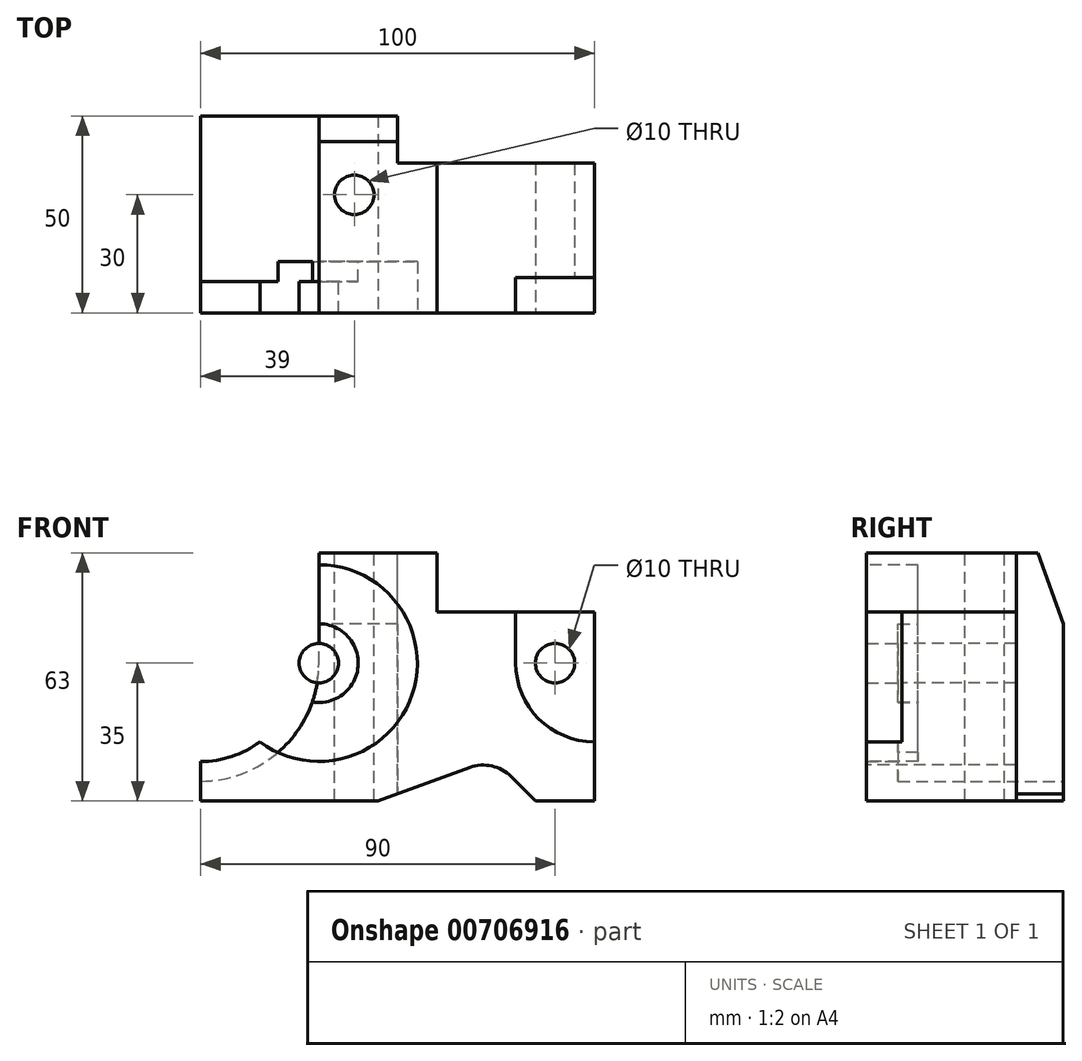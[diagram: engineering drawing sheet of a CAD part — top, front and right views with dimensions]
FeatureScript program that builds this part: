
annotation { "Feature Type Name" : "Feature", "Feature Type Description" : "" }
export const myFeature = defineFeature(function(context is Context, id is Id, definition is map)
    precondition{}
    {
        {
            var Q0;
            Q0=qCreatedBy(makeId("Front.planeOp"),FACE);
            var sketch = newSketch(context, id + "F0", { "sketchPlane" : qUnion([Q0])});
            skLineSegment(sketch, "E0", {"start": v(0, 0) * mm, "end": v(100, 0) * mm});
            skLineSegment(sketch, "E1", {"start": v(100, 0) * mm, "end": v(100, 63) * mm});
            skLineSegment(sketch, "E2", {"start": v(100, 63) * mm, "end": v(0, 63) * mm});
            skLineSegment(sketch, "E3", {"start": v(0, 63) * mm, "end": v(0, 0) * mm});
            skSolve(sketch);
        }
        {
            var Q0;
            Q0 = qSketchRegion(id + "F0", true);
            extrude(context, id + "F1", {"entities" : qUnion([Q0]), "depth" : 50 * mm, "offsetDistance" : 25 * mm});
        }
        {
            var Q0;
            Q0=makeQuery(id+"F1.opExtrude","CAP_FACE",FACE,{"disambiguationData":[OSD([sQuery(id+"F0.wireOp",EDGE,"E0"),sQuery(id+"F0.wireOp",EDGE,"E1"),sQuery(id+"F0.wireOp",EDGE,"E2"),sQuery(id+"F0.wireOp",EDGE,"E3")])],"isStart":false});
            var sketch = newSketch(context, id + "F2", { "sketchPlane" : qUnion([Q0])});
            skLineSegment(sketch, "E4", {"start": v(100, 48) * mm, "end": v(60, 48) * mm});
            skLineSegment(sketch, "E5", {"start": v(60, 48) * mm, "end": v(60, 63) * mm});
            skLineSegment(sketch, "E6", {"start": v(60, 63) * mm, "end": v(100, 63) * mm});
            skLineSegment(sketch, "E7", {"start": v(100, 63) * mm, "end": v(100, 48) * mm});
            skSolve(sketch);
        }
        {
            var Q0;
            Q0 = qSketchRegion(id + "F2", true);
            extrude(context, id + "F3", {"entities" : qUnion([Q0]), "operationType" : NewBodyOperationType.REMOVE, "endBound" : BoundingType.THROUGH_ALL, "oppositeDirection" : true, "depth" : 25 * mm, "offsetDistance" : 25 * mm});
        }
        {
            var Q0;
            Q0=makeQuery(id+"F1.opExtrude","CAP_FACE",FACE,{"disambiguationData":[OSD([sQuery(id+"F0.wireOp",EDGE,"E0"),sQuery(id+"F0.wireOp",EDGE,"E1"),sQuery(id+"F0.wireOp",EDGE,"E2"),sQuery(id+"F0.wireOp",EDGE,"E3")])],"isStart":true});
            var sketch = newSketch(context, id + "F4", { "sketchPlane" : qUnion([Q0])});
            skCircle(sketch, "E8", {"center": v(0, 35) * mm, "radius": 30 * mm});
            skLineSegment(sketch, "E9", {"start": v(-30, 35) * mm, "end": v(-30, 65) * mm});
            skLineSegment(sketch, "E10", {"start": v(-30, 65) * mm, "end": v(0, 65) * mm});
            skSolve(sketch);
        }
        {
            var Q0;
            Q0 = qSketchRegion(id + "F4", true);
            extrude(context, id + "F5", {"entities" : qUnion([Q0]), "operationType" : NewBodyOperationType.REMOVE, "oppositeDirection" : true, "depth" : 42 * mm, "offsetDistance" : 25 * mm});
        }
        {
            var Q0;
            Q0=makeQuery(id+"F1.opExtrude","CAP_FACE",FACE,{"disambiguationData":[OSD([sQuery(id+"F0.wireOp",EDGE,"E0"),sQuery(id+"F0.wireOp",EDGE,"E1"),sQuery(id+"F0.wireOp",EDGE,"E2"),sQuery(id+"F0.wireOp",EDGE,"E3")])],"isStart":true});
            var sketch = newSketch(context, id + "F6", { "sketchPlane" : qUnion([Q0])});
            skArc(sketch, "E11.0", {"start": v(-30, 35) * mm, "mid": v(-21.21, 13.79) * mm, "end": v(0, 5) * mm});
            skCircle(sketch, "E12", {"center": v(0, 35) * mm, "radius": 25 * mm});
            skSolve(sketch);
        }
        {
            var Q0;
            Q0 = qSketchRegion(id + "F6", true);
            extrude(context, id + "F7", {"entities" : qUnion([Q0]), "operationType" : NewBodyOperationType.REMOVE, "endBound" : BoundingType.THROUGH_ALL, "oppositeDirection" : true, "depth" : 25 * mm, "offsetDistance" : 25 * mm});
        }
        {
            var Q0;
            Q0=makeQuery(id+"F1.opExtrude","CAP_FACE",FACE,{"disambiguationData":[OSD([sQuery(id+"F0.wireOp",EDGE,"E0"),sQuery(id+"F0.wireOp",EDGE,"E1"),sQuery(id+"F0.wireOp",EDGE,"E2"),sQuery(id+"F0.wireOp",EDGE,"E3")])],"isStart":true});
            var sketch = newSketch(context, id + "F8", { "sketchPlane" : qUnion([Q0])});
            skLineSegment(sketch, "E13.0", {"start": v(-30, 35) * mm, "end": v(-30, 63) * mm});
            skLineSegment(sketch, "E14", {"start": v(-30, 63) * mm, "end": v(3.42, 63) * mm});
            skLineSegment(sketch, "E15", {"start": v(3.42, 63) * mm, "end": v(3.42, 35) * mm});
            skLineSegment(sketch, "E16", {"start": v(3.42, 35) * mm, "end": v(-30, 35) * mm});
            skSolve(sketch);
        }
        {
            var Q0;
            Q0 = qSketchRegion(id + "F8", true);
            extrude(context, id + "F9", {"entities" : qUnion([Q0]), "operationType" : NewBodyOperationType.REMOVE, "endBound" : BoundingType.THROUGH_ALL, "oppositeDirection" : true, "depth" : 25 * mm, "offsetDistance" : 25 * mm});
        }
        {
            var Q0;
            Q0=makeQuery(id+"F1.opExtrude","CAP_FACE",FACE,{"disambiguationData":[OSD([sQuery(id+"F0.wireOp",EDGE,"E0"),sQuery(id+"F0.wireOp",EDGE,"E1"),sQuery(id+"F0.wireOp",EDGE,"E2"),sQuery(id+"F0.wireOp",EDGE,"E3")])],"isStart":false});
            var sketch = newSketch(context, id + "F10", { "sketchPlane" : qUnion([Q0])});
            skCircle(sketch, "E17", {"center": v(30, 35) * mm, "radius": 25 * mm});
            skSolve(sketch);
        }
        {
            var Q0;
            Q0 = qSketchRegion(id + "F10", true);
            extrude(context, id + "F11", {"entities" : qUnion([Q0]), "operationType" : NewBodyOperationType.REMOVE, "oppositeDirection" : true, "depth" : 13 * mm, "offsetDistance" : 25 * mm});
        }
        {
            var Q0;
            Q0=makeQuery(id+"F11.boolean.opBoolean","COPY",FACE,{"derivedFrom":makeQuery(id+"F11.opExtrude","CAP_FACE",FACE,{"disambiguationData":[OSD([sQuery(id+"F10.wireOp",EDGE,"E17")])],"isStart":false})});
            var sketch = newSketch(context, id + "F12", { "sketchPlane" : qUnion([Q0])});
            skCircle(sketch, "E18", {"center": v(30, 35) * mm, "radius": 10 * mm});
            skSolve(sketch);
        }
        {
            var Q0;
            Q0 = qSketchRegion(id + "F12", true);
            extrude(context, id + "F13", {"entities" : qUnion([Q0]), "operationType" : NewBodyOperationType.ADD, "depth" : 5 * mm, "offsetDistance" : 25 * mm});
        }
        {
            var Q0;
            Q0 = qSketchRegion(id + "F4", true);
            extrude(context, id + "F14", {"entities" : qUnion([Q0]), "operationType" : NewBodyOperationType.REMOVE, "oppositeDirection" : true, "depth" : 42 * mm, "offsetDistance" : 25 * mm});
        }
        {
            var Q0;
            Q0=makeQuery(id+"F13.opExtrude","CAP_FACE",FACE,{"disambiguationData":[OSD([sQuery(id+"F12.wireOp",EDGE,"E18")])],"isStart":false});
            var sketch = newSketch(context, id + "F15", { "sketchPlane" : qUnion([Q0])});
            skCircle(sketch, "E19", {"center": v(30, 35) * mm, "radius": 5 * mm});
            skSolve(sketch);
        }
        {
            var Q0;
            Q0 = qSketchRegion(id + "F15", true);
            extrude(context, id + "F16", {"entities" : qUnion([Q0]), "operationType" : NewBodyOperationType.ADD, "depth" : 8 * mm, "offsetDistance" : 25 * mm});
        }
        {
            var Q0;
            {var subQ0=sQuery(id+"F4.wireOp",EDGE,"E9");Q0=makeQuery(id+"F14.boolean.opBoolean","MERGE",FACE,{"derivedFrom":[makeQuery(id+"F9.boolean.opBoolean","MERGE",FACE,{"derivedFrom":[makeQuery(id+"F5.boolean.opBoolean","COPY",FACE,{"derivedFrom":makeQuery(id+"F5.opExtrude","SWEPT_FACE",FACE,{"disambiguationData":[OSD([subQ0])]})}),makeQuery(id+"F9.opExtrude","SWEPT_FACE",FACE,{"disambiguationData":[OSD([sQuery(id+"F8.wireOp",EDGE,"E13.0")])]})]}),makeQuery(id+"F14.opExtrude","SWEPT_FACE",FACE,{"disambiguationData":[OSD([subQ0])]})]});}
            var sketch = newSketch(context, id + "F17", { "sketchPlane" : qUnion([Q0])});
            skLineSegment(sketch, "E20", {"start": v(0, 63) * mm, "end": v(0, 45) * mm});
            skLineSegment(sketch, "E21", {"start": v(0, 45) * mm, "end": v(6.55, 63) * mm});
            skLineSegment(sketch, "E22", {"start": v(6.55, 63) * mm, "end": v(0, 63) * mm});
            skSolve(sketch);
        }
        {
            var Q0;
            Q0 = qSketchRegion(id + "F17", true);
            extrude(context, id + "F18", {"entities" : qUnion([Q0]), "operationType" : NewBodyOperationType.REMOVE, "endBound" : BoundingType.THROUGH_ALL, "oppositeDirection" : true, "depth" : 25 * mm, "offsetDistance" : 25 * mm});
        }
        {
            var Q0;
            Q0=makeQuery(id+"F1.opExtrude","SWEPT_FACE",FACE,{"disambiguationData":[OSD([sQuery(id+"F0.wireOp",EDGE,"E1")])]});
            var sketch = newSketch(context, id + "F19", { "sketchPlane" : qUnion([Q0])});
            skLineSegment(sketch, "E23", {"start": v(0, 0) * mm, "end": v(-12, 0) * mm});
            skLineSegment(sketch, "E24", {"start": v(-12, 0) * mm, "end": v(-12, 63.23) * mm});
            skLineSegment(sketch, "E25", {"start": v(-12, 63.23) * mm, "end": v(0, 63.23) * mm});
            skLineSegment(sketch, "E26", {"start": v(0, 63.23) * mm, "end": v(0, 0) * mm});
            skSolve(sketch);
        }
        {
            var Q0;
            Q0 = qSketchRegion(id + "F19", true);
            extrude(context, id + "F20", {"entities" : qUnion([Q0]), "operationType" : NewBodyOperationType.REMOVE, "oppositeDirection" : true, "depth" : 50 * mm, "offsetDistance" : 25 * mm});
        }
        {
            var Q0;
            Q0=makeQuery(id+"F1.opExtrude","CAP_FACE",FACE,{"disambiguationData":[OSD([sQuery(id+"F0.wireOp",EDGE,"E0"),sQuery(id+"F0.wireOp",EDGE,"E1"),sQuery(id+"F0.wireOp",EDGE,"E2"),sQuery(id+"F0.wireOp",EDGE,"E3")])],"isStart":false});
            var sketch = newSketch(context, id + "F21", { "sketchPlane" : qUnion([Q0])});
            skCircle(sketch, "E27", {"center": v(100, 35) * mm, "radius": 20 * mm});
            skLineSegment(sketch, "E28", {"start": v(80, 35) * mm, "end": v(80, 48) * mm});
            skLineSegment(sketch, "E29", {"start": v(80, 48) * mm, "end": v(84.8, 48) * mm});
            skSolve(sketch);
        }
        {
            var Q0;
            Q0 = qSketchRegion(id + "F21", true);
            extrude(context, id + "F22", {"entities" : qUnion([Q0]), "operationType" : NewBodyOperationType.REMOVE, "oppositeDirection" : true, "depth" : 9 * mm, "offsetDistance" : 25 * mm});
        }
        {
            var Q0;
            Q0=makeQuery(id+"F22.boolean.opBoolean","COPY",FACE,{"derivedFrom":makeQuery(id+"F22.opExtrude","CAP_FACE",FACE,{"disambiguationData":[OSD([sQuery(id+"F21.wireOp",EDGE,"E27"),sQuery(id+"F21.wireOp",EDGE,"E28"),sQuery(id+"F21.wireOp",EDGE,"E29")])],"isStart":false})});
            var sketch = newSketch(context, id + "F23", { "sketchPlane" : qUnion([Q0])});
            skArc(sketch, "E30.0", {"start": v(80, 35) * mm, "mid": v(85.86, 20.86) * mm, "end": v(100, 15) * mm, "construction": true});
            skLineSegment(sketch, "E31", {"start": v(100, 35) * mm, "end": v(80, 35) * mm, "construction": true});
            skCircle(sketch, "E32", {"center": v(90, 35) * mm, "radius": 5 * mm});
            skSolve(sketch);
        }
        {
            var Q0;
            Q0 = qSketchRegion(id + "F23", true);
            extrude(context, id + "F24", {"entities" : qUnion([Q0]), "operationType" : NewBodyOperationType.REMOVE, "endBound" : BoundingType.THROUGH_ALL, "oppositeDirection" : true, "depth" : 25 * mm, "offsetDistance" : 25 * mm});
        }
        {
            var Q0;
            Q0=makeQuery(id+"F1.opExtrude","SWEPT_FACE",FACE,{"disambiguationData":[OSD([sQuery(id+"F0.wireOp",EDGE,"E2")])]});
            var sketch = newSketch(context, id + "F25", { "sketchPlane" : qUnion([Q0])});
            skCircle(sketch, "E33", {"center": v(39, -20) * mm, "radius": 5 * mm});
            skSolve(sketch);
        }
        {
            var Q0;
            Q0 = qSketchRegion(id + "F25", true);
            extrude(context, id + "F26", {"entities" : qUnion([Q0]), "operationType" : NewBodyOperationType.REMOVE, "endBound" : BoundingType.THROUGH_ALL, "oppositeDirection" : true, "depth" : 25 * mm, "offsetDistance" : 25 * mm});
        }
        {
            var Q0;
            Q0=makeQuery(id+"F1.opExtrude","CAP_FACE",FACE,{"disambiguationData":[OSD([sQuery(id+"F0.wireOp",EDGE,"E0"),sQuery(id+"F0.wireOp",EDGE,"E1"),sQuery(id+"F0.wireOp",EDGE,"E2"),sQuery(id+"F0.wireOp",EDGE,"E3")])],"isStart":false});
            var sketch = newSketch(context, id + "F27", { "sketchPlane" : qUnion([Q0])});
            skLineSegment(sketch, "E34", {"start": v(45, 0) * mm, "end": v(68.34, 8.5) * mm});
            skLineSegment(sketch, "E35", {"start": v(78.83, 6.17) * mm, "end": v(85, 0) * mm});
            skLineSegment(sketch, "E36", {"start": v(85, 0) * mm, "end": v(45, 0) * mm});
            skPoint(sketch, "E37.visualSharp", {"position": v(74.33, 10.67) * mm});
            skArc(sketch, "E37.filletArc", {"start": v(78.83, 6.17) * mm, "mid": v(73.92, 8.86) * mm, "end": v(68.34, 8.5) * mm});
            skSolve(sketch);
        }
        {
            var Q0;
            Q0 = qSketchRegion(id + "F27", true);
            extrude(context, id + "F28", {"entities" : qUnion([Q0]), "operationType" : NewBodyOperationType.REMOVE, "endBound" : BoundingType.THROUGH_ALL, "oppositeDirection" : true, "depth" : 25 * mm, "offsetDistance" : 25 * mm});
        }
    });
